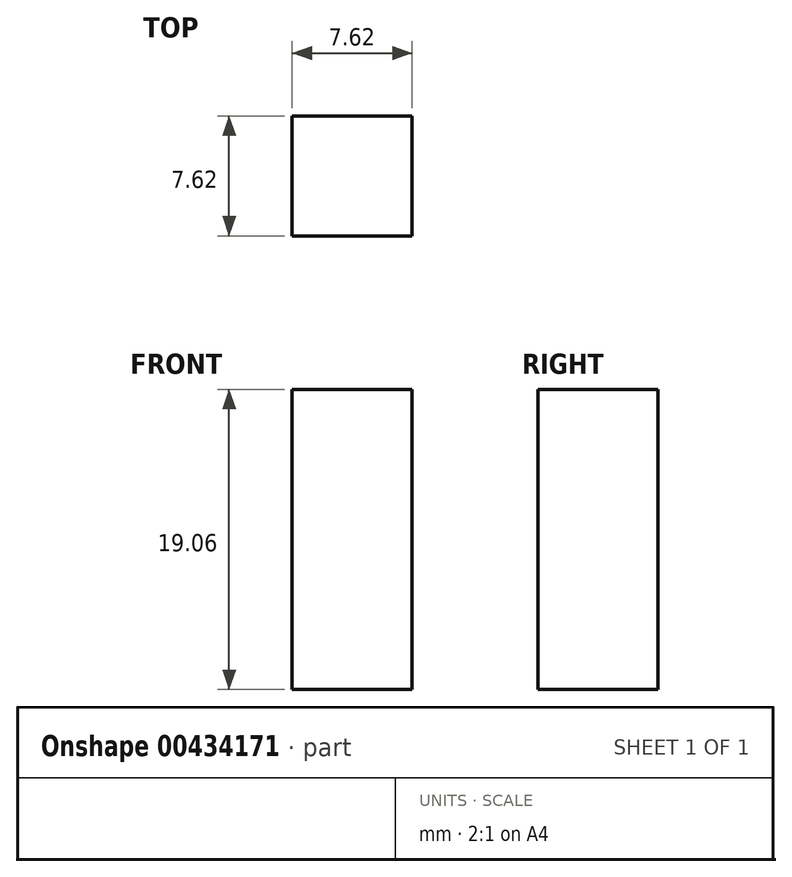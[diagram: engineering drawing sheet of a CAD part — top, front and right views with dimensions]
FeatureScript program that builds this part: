
annotation { "Feature Type Name" : "Feature", "Feature Type Description" : "" }
export const myFeature = defineFeature(function(context is Context, id is Id, definition is map)
    precondition{}
    {
        {
            var Q0;
            Q0=qCreatedBy(makeId("Front.planeOp"),FACE);
            var sketch = newSketch(context, id + "F0", { "sketchPlane" : qUnion([Q0])});
            skLineSegment(sketch, "E0.bottom", {"start": v(-3.81, 9.53) * mm, "end": v(3.8, 9.53) * mm});
            skLineSegment(sketch, "E0.top", {"start": v(-3.8, -9.53) * mm, "end": v(3.81, -9.53) * mm});
            skLineSegment(sketch, "E0.left", {"start": v(-3.81, 9.52) * mm, "end": v(-3.8, -9.53) * mm});
            skLineSegment(sketch, "E0.right", {"start": v(3.8, 9.53) * mm, "end": v(3.81, -9.52) * mm});
            skPoint(sketch, "E0.middle", {"position": v(0, 0) * mm});
            skSolve(sketch);
        }
        {
            var Q0;
            Q0=makeQuery(id+"F0.imprint","IMPRINT",FACE,{"disambiguationData":[TD([[makeQuery(id+"F0.imprint","IMPRINT",EDGE,{"derivedFrom":sQuery(id+"F0.wireOp",EDGE,"E0.bottom")}),-1.0]])]});
            extrude(context, id + "F1", {"entities" : qUnion([Q0]), "depth" : 7.62 * mm});
        }
    });
